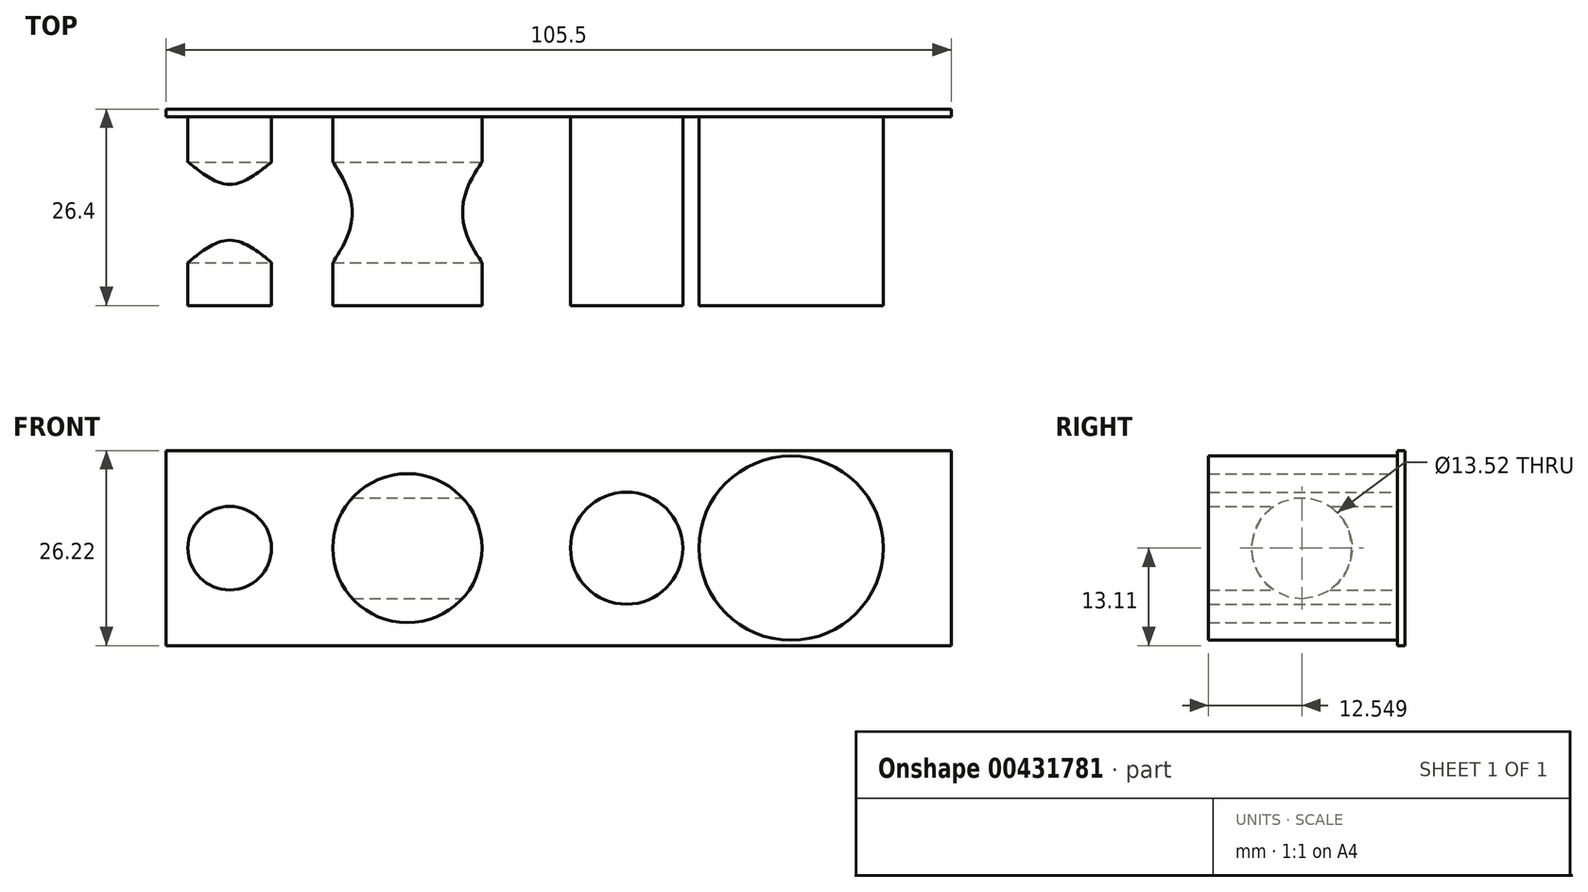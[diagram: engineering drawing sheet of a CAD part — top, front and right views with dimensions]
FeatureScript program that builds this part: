
annotation { "Feature Type Name" : "Feature", "Feature Type Description" : "" }
export const myFeature = defineFeature(function(context is Context, id is Id, definition is map)
    precondition{}
    {
        {
            var Q0;
            Q0=qCreatedBy(makeId("Front.planeOp"),FACE);
            var sketch = newSketch(context, id + "F0", { "sketchPlane" : qUnion([Q0])});
            skLineSegment(sketch, "E0.bottom", {"start": v(52.75, 13.11) * mm, "end": v(-52.75, 13.11) * mm});
            skLineSegment(sketch, "E0.top", {"start": v(52.75, -13.11) * mm, "end": v(-52.75, -13.11) * mm});
            skLineSegment(sketch, "E0.left", {"start": v(52.75, 13.11) * mm, "end": v(52.75, -13.11) * mm});
            skLineSegment(sketch, "E0.right", {"start": v(-52.75, 13.11) * mm, "end": v(-52.75, -13.11) * mm});
            skPoint(sketch, "E0.middle", {"position": v(0, 0) * mm});
            skSolve(sketch);
        }
        {
            var Q0;
            Q0=makeQuery(id+"F0.imprint","IMPRINT",FACE,{"disambiguationData":[TD([[makeQuery(id+"F0.imprint","IMPRINT",EDGE,{"derivedFrom":sQuery(id+"F0.wireOp",EDGE,"E0.bottom")}),1.0]])]});
            extrude(context, id + "F1", {"entities" : qUnion([Q0]), "depth" : 1 * mm});
        }
        {
            var Q0;
            Q0=makeQuery(id+"F1.opExtrude","CAP_FACE",FACE,{"disambiguationData":[OSD([sQuery(id+"F0.wireOp",EDGE,"E0.bottom"),sQuery(id+"F0.wireOp",EDGE,"E0.top"),sQuery(id+"F0.wireOp",EDGE,"E0.left"),sQuery(id+"F0.wireOp",EDGE,"E0.right")])],"isStart":false});
            var sketch = newSketch(context, id + "F2", { "sketchPlane" : qUnion([Q0])});
            skCircle(sketch, "E1", {"center": v(-44.2, 0) * mm, "radius": 5.62 * mm});
            skCircle(sketch, "E2", {"center": v(-20.33, 0) * mm, "radius": 10.02 * mm});
            skCircle(sketch, "E3", {"center": v(9.14, 0) * mm, "radius": 7.54 * mm});
            skCircle(sketch, "E4", {"center": v(31.24, 0) * mm, "radius": 12.39 * mm});
            skSolve(sketch);
        }
        {
            var Q0;
            Q0=makeQuery(id+"F2.imprint","IMPRINT",FACE,{"disambiguationData":[TD([[makeQuery(id+"F2.imprint","IMPRINT",EDGE,{"derivedFrom":sQuery(id+"F2.wireOp",EDGE,"E1")}),1.0]])]});
            var Q1;
            Q1=makeQuery(id+"F2.imprint","IMPRINT",FACE,{"disambiguationData":[TD([[makeQuery(id+"F2.imprint","IMPRINT",EDGE,{"derivedFrom":sQuery(id+"F2.wireOp",EDGE,"E2")}),1.0]])]});
            var Q2;
            Q2=makeQuery(id+"F2.imprint","IMPRINT",FACE,{"disambiguationData":[TD([[makeQuery(id+"F2.imprint","IMPRINT",EDGE,{"derivedFrom":sQuery(id+"F2.wireOp",EDGE,"E3")}),1.0]])]});
            var Q3;
            Q3=makeQuery(id+"F2.imprint","IMPRINT",FACE,{"disambiguationData":[TD([[makeQuery(id+"F2.imprint","IMPRINT",EDGE,{"derivedFrom":sQuery(id+"F2.wireOp",EDGE,"E4")}),1.0]])]});
            extrude(context, id + "F3", {"entities" : qUnion([Q0, Q1, Q2, Q3]), "operationType" : NewBodyOperationType.ADD, "depth" : 25.4 * mm});
        }
        {
            var Q0;
            Q0=qCreatedBy(makeId("Right.planeOp"),FACE);
            var sketch = newSketch(context, id + "F4", { "sketchPlane" : qUnion([Q0])});
            skCircle(sketch, "E5", {"center": v(-13.85, 0) * mm, "radius": 6.76 * mm});
            skSolve(sketch);
        }
        {
            var Q0;
            Q0=makeQuery(id+"F4.imprint","IMPRINT",FACE,{"disambiguationData":[TD([[makeQuery(id+"F4.imprint","IMPRINT",EDGE,{"derivedFrom":sQuery(id+"F4.wireOp",EDGE,"E5")}),1.0]])]});
            extrude(context, id + "F5", {"entities" : qUnion([Q0]), "operationType" : NewBodyOperationType.REMOVE, "oppositeDirection" : true, "depth" : 99.57 * mm});
        }
    });
